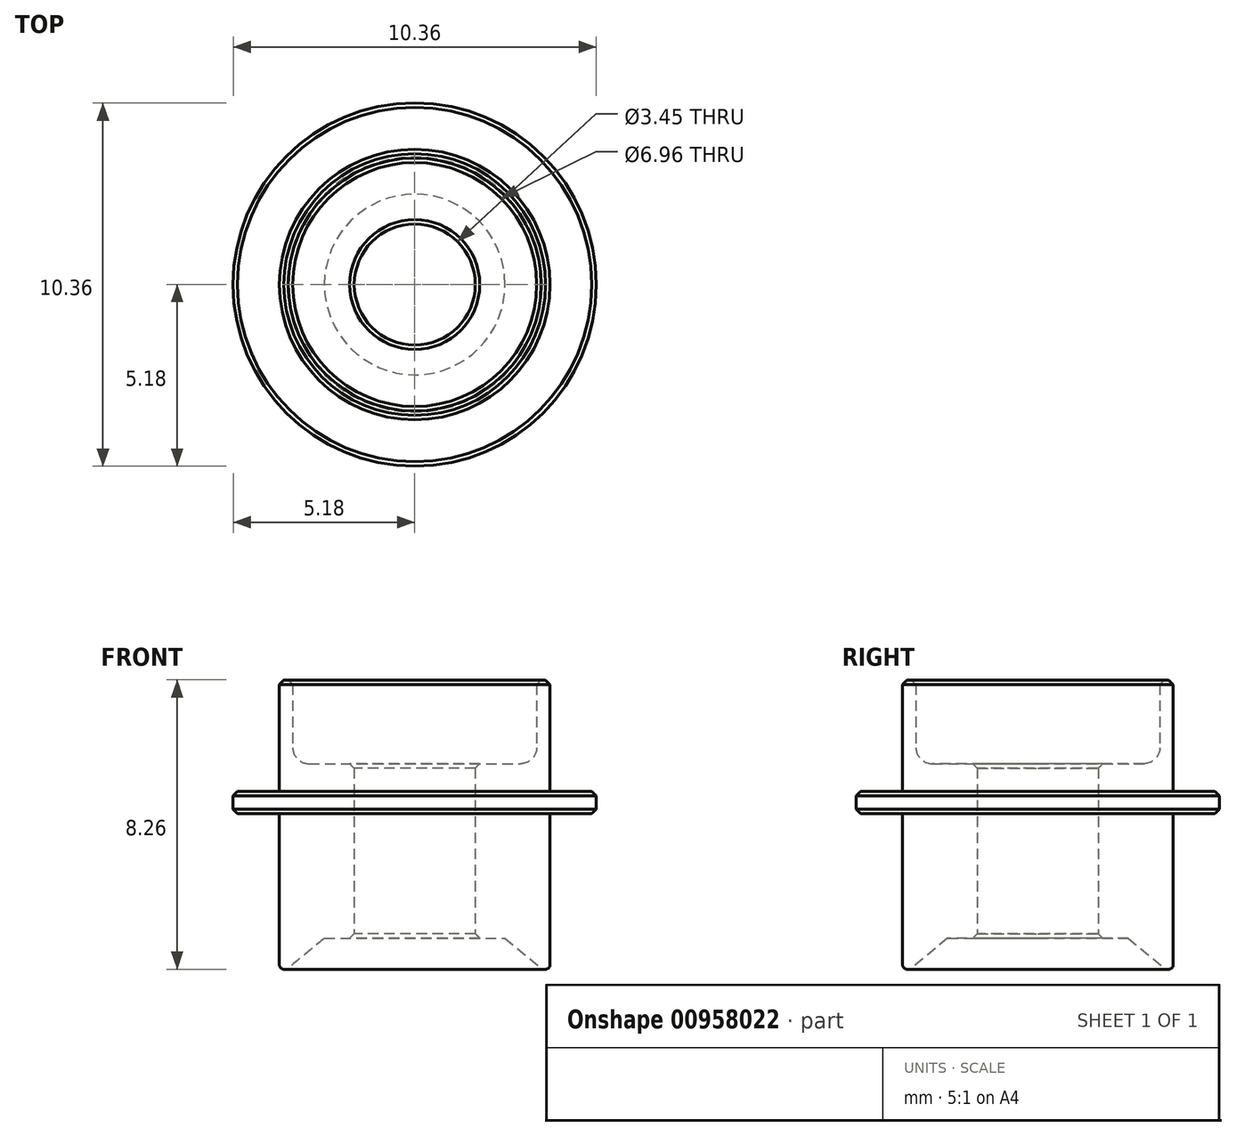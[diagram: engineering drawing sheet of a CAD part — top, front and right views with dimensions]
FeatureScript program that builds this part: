
annotation { "Feature Type Name" : "Feature", "Feature Type Description" : "" }
export const myFeature = defineFeature(function(context is Context, id is Id, definition is map)
    precondition{}
    {
        {
            var Q0;
            Q0=qCreatedBy(makeId("Front.planeOp"),FACE);
            var sketch = newSketch(context, id + "F0", { "sketchPlane" : qUnion([Q0])});
            skLineSegment(sketch, "E0", {"start": v(3.48, 8.26) * mm, "end": v(3.86, 8.26) * mm});
            skLineSegment(sketch, "E1", {"start": v(3.86, 8.26) * mm, "end": v(3.86, 5.08) * mm});
            skLineSegment(sketch, "E2", {"start": v(3.86, 5.08) * mm, "end": v(5.18, 5.08) * mm});
            skLineSegment(sketch, "E3", {"start": v(5.18, 5.08) * mm, "end": v(5.18, 4.45) * mm});
            skLineSegment(sketch, "E4", {"start": v(5.18, 4.45) * mm, "end": v(3.86, 4.45) * mm});
            skLineSegment(sketch, "E5", {"start": v(3.86, 4.45) * mm, "end": v(3.86, 0) * mm});
            skLineSegment(sketch, "E6", {"start": v(3.48, 8.26) * mm, "end": v(3.48, 6.32) * mm});
            skLineSegment(sketch, "E7", {"start": v(3.02, 5.87) * mm, "end": v(1.73, 5.87) * mm});
            skArc(sketch, "E8.filletArc", {"start": v(3.02, 5.87) * mm, "mid": v(3.35, 6) * mm, "end": v(3.48, 6.32) * mm});
            skLineSegment(sketch, "E9", {"start": v(2.58, 0.89) * mm, "end": v(1.73, 0.89) * mm});
            skLineSegment(sketch, "E10", {"start": v(1.73, 0.89) * mm, "end": v(1.73, 5.87) * mm});
            skLineSegment(sketch, "E11", {"start": v(0, 0) * mm, "end": v(0, 15.49) * mm, "construction": true});
            skLineSegment(sketch, "E12", {"start": v(2.58, 0.89) * mm, "end": v(3.64, 0) * mm});
            skLineSegment(sketch, "E13", {"start": v(3.64, 0) * mm, "end": v(3.86, 0) * mm});
            skPoint(sketch, "E14.orphan", {"position": v(1.03, 5.87) * mm});
            skSolve(sketch);
        }
        {
            var Q0;
            Q0 = qSketchRegion(id + "F0", true);
            var Q1;
            Q1=sQuery(id+"F0.wireOp",EDGE,"E11");
            revolve(context, id + "F1", {"surfaceOperationType" : NewSurfaceOperationType.NEW, "entities" : qUnion([Q0]), "axis" : qUnion([Q1]), "revolveType" : RevolveType.FULL});
        }
        {
            var Q0;
            Q0=makeQuery(id+"F1.opRevolve","SWEPT_EDGE",EDGE,{"disambiguationData":[OSD([sQuery(id+"F0.wireOp",EDGE,"E5"),sQuery(id+"F0.wireOp",EDGE,"E13")])]});
            fillet(context, id + "F2", {"entities" : qUnion([Q0]), "radius" : 0.13 * mm, "tangentPropagation" : true, "allowEdgeOverflow" : false});
        }
        {
            var Q0;
            Q0=makeQuery(id+"F1.opRevolve","SWEPT_EDGE",EDGE,{"disambiguationData":[OSD([sQuery(id+"F0.wireOp",EDGE,"E9"),sQuery(id+"F0.wireOp",EDGE,"E10")])]});
            chamfer(context, id + "F3", {"entities" : qUnion([Q0]), "width" : 0.13 * mm, "tangentPropagation" : true});
        }
        {
            var Q0;
            Q0=makeQuery(id+"F1.opRevolve","SWEPT_EDGE",EDGE,{"disambiguationData":[OSD([sQuery(id+"F0.wireOp",EDGE,"E7"),sQuery(id+"F0.wireOp",EDGE,"E10")])]});
            var Q1;
            Q1=makeQuery(id+"F1.opRevolve","SWEPT_EDGE",EDGE,{"disambiguationData":[OSD([sQuery(id+"F0.wireOp",EDGE,"E0"),sQuery(id+"F0.wireOp",EDGE,"E6")])]});
            var Q2;
            Q2=makeQuery(id+"F1.opRevolve","SWEPT_EDGE",EDGE,{"disambiguationData":[OSD([sQuery(id+"F0.wireOp",EDGE,"E0"),sQuery(id+"F0.wireOp",EDGE,"E1")])]});
            var Q3;
            Q3=makeQuery(id+"F1.opRevolve","SWEPT_EDGE",EDGE,{"disambiguationData":[OSD([sQuery(id+"F0.wireOp",EDGE,"E2"),sQuery(id+"F0.wireOp",EDGE,"E3")])]});
            var Q4;
            Q4=makeQuery(id+"F1.opRevolve","SWEPT_EDGE",EDGE,{"disambiguationData":[OSD([sQuery(id+"F0.wireOp",EDGE,"E3"),sQuery(id+"F0.wireOp",EDGE,"E4")])]});
            chamfer(context, id + "F4", {"entities" : qUnion([Q0, Q1, Q2, Q3, Q4]), "width" : 0.13 * mm, "tangentPropagation" : true});
        }
    });
